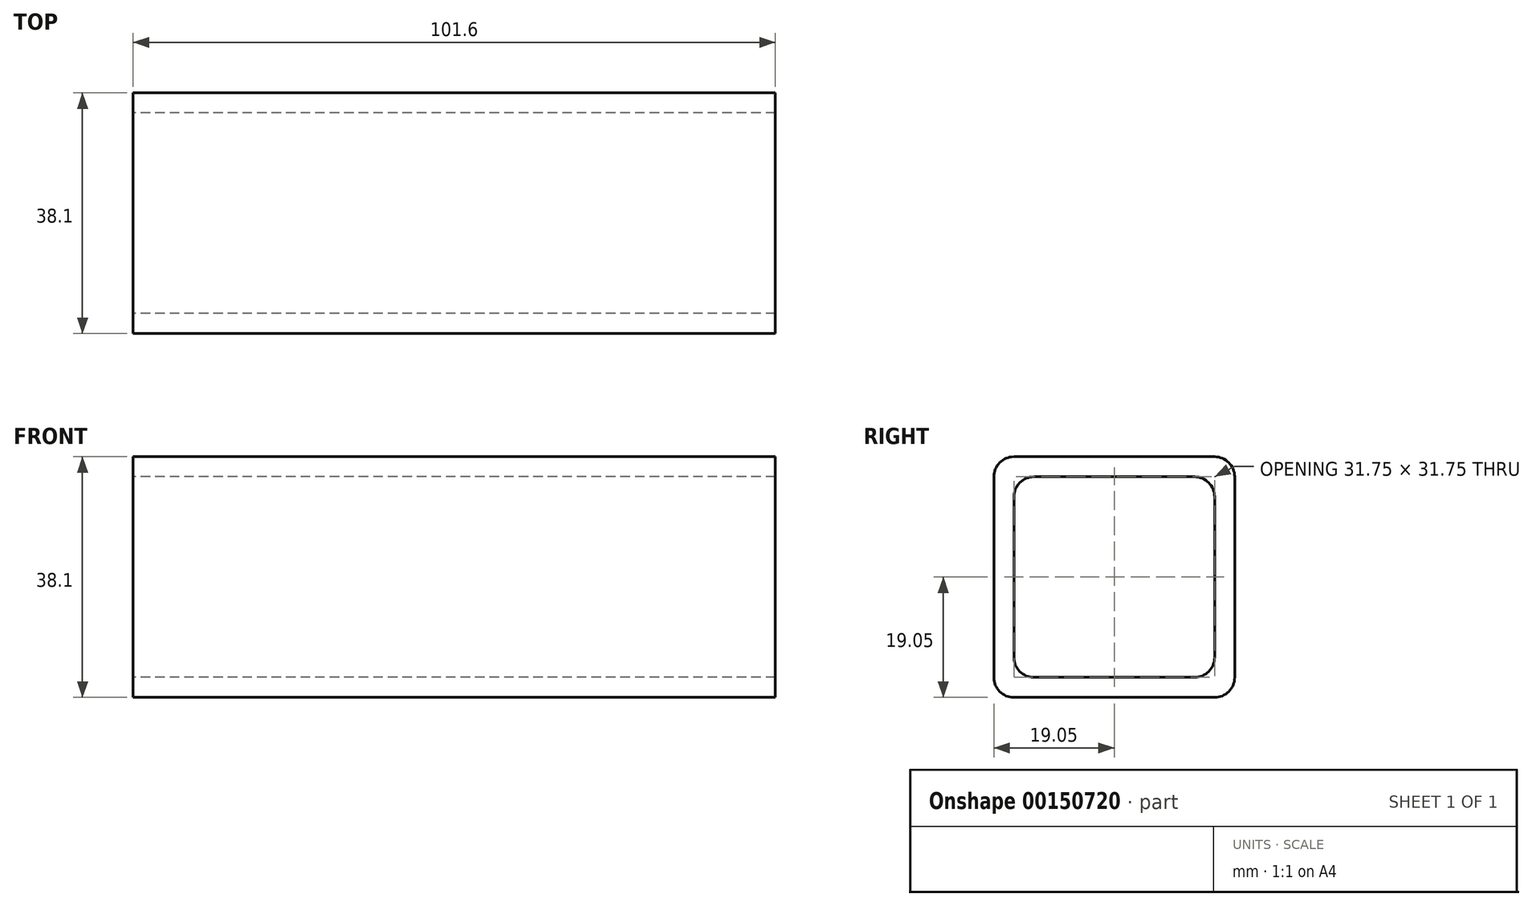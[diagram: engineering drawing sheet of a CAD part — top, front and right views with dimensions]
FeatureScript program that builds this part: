
annotation { "Feature Type Name" : "Feature", "Feature Type Description" : "" }
export const myFeature = defineFeature(function(context is Context, id is Id, definition is map)
    precondition{}
    {
        {
            var Q0;
            Q0=qCreatedBy(makeId("Right.planeOp"),FACE);
            var sketch = newSketch(context, id + "F0", { "sketchPlane" : qUnion([Q0])});
            skLineSegment(sketch, "E0.bottom", {"start": v(15.87, 19.05) * mm, "end": v(-15.88, 19.05) * mm});
            skLineSegment(sketch, "E0.top", {"start": v(15.88, -19.05) * mm, "end": v(-15.87, -19.05) * mm});
            skLineSegment(sketch, "E0.left", {"start": v(19.05, 15.88) * mm, "end": v(19.05, -15.88) * mm});
            skLineSegment(sketch, "E0.right", {"start": v(-19.05, 15.87) * mm, "end": v(-19.05, -15.88) * mm});
            skPoint(sketch, "E0.middle", {"position": v(0, 0) * mm});
            skPoint(sketch, "E1.visualSharp", {"position": v(-19.05, 19.05) * mm});
            skArc(sketch, "E1.filletArc", {"start": v(-15.88, 19.05) * mm, "mid": v(-18.12, 18.12) * mm, "end": v(-19.05, 15.87) * mm});
            skPoint(sketch, "E2.visualSharp", {"position": v(19.05, 19.05) * mm});
            skArc(sketch, "E2.filletArc", {"start": v(19.05, 15.88) * mm, "mid": v(18.12, 18.12) * mm, "end": v(15.87, 19.05) * mm});
            skPoint(sketch, "E3.visualSharp", {"position": v(-19.05, -19.05) * mm});
            skArc(sketch, "E3.filletArc", {"start": v(-19.05, -15.88) * mm, "mid": v(-18.12, -18.12) * mm, "end": v(-15.87, -19.05) * mm});
            skPoint(sketch, "E4.visualSharp", {"position": v(19.05, -19.05) * mm});
            skArc(sketch, "E4.filletArc", {"start": v(15.88, -19.05) * mm, "mid": v(18.12, -18.12) * mm, "end": v(19.05, -15.88) * mm});
            skLineSegment(sketch, "E5.bottom", {"start": v(12.7, 15.88) * mm, "end": v(-12.7, 15.88) * mm});
            skLineSegment(sketch, "E5.top", {"start": v(12.7, -15.88) * mm, "end": v(-12.7, -15.88) * mm});
            skLineSegment(sketch, "E5.left", {"start": v(15.87, 12.7) * mm, "end": v(15.88, -12.7) * mm});
            skLineSegment(sketch, "E5.right", {"start": v(-15.88, 12.7) * mm, "end": v(-15.87, -12.7) * mm});
            skArc(sketch, "E6.filletArc", {"start": v(-12.7, 15.88) * mm, "mid": v(-14.95, 14.95) * mm, "end": v(-15.88, 12.7) * mm});
            skArc(sketch, "E7.filletArc", {"start": v(15.88, 12.7) * mm, "mid": v(14.95, 14.95) * mm, "end": v(12.7, 15.88) * mm});
            skArc(sketch, "E8.filletArc", {"start": v(-15.88, -12.7) * mm, "mid": v(-14.95, -14.95) * mm, "end": v(-12.7, -15.88) * mm});
            skPoint(sketch, "E9.visualSharp", {"position": v(15.88, -15.87) * mm});
            skArc(sketch, "E9.filletArc", {"start": v(12.7, -15.88) * mm, "mid": v(14.95, -14.95) * mm, "end": v(15.88, -12.7) * mm});
            skSolve(sketch);
        }
        {
            var Q0;
            Q0=qSketchRegion(id+"F0",true);
            extrude(context, id + "F1", {"entities" : qUnion([Q0]), "depth" : 101.6 * mm});
        }
    });
